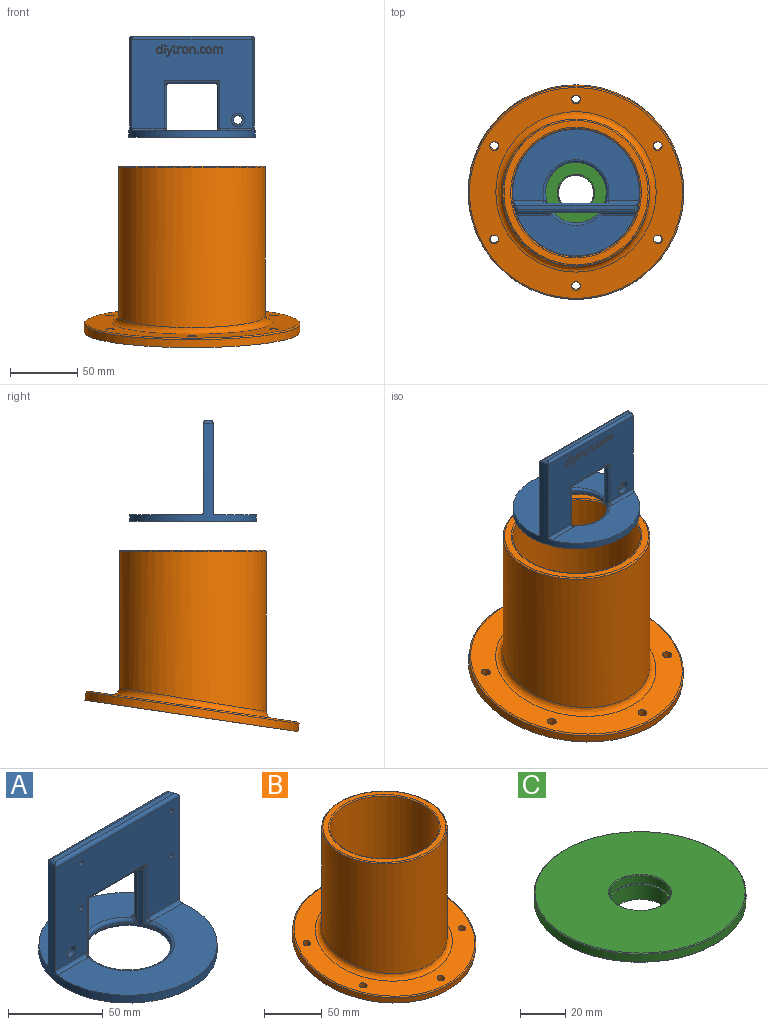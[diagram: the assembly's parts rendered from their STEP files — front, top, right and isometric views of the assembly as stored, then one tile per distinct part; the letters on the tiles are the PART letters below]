
ASSEMBLY  parts=3 mates=2
PART A: 256 faces, bbox 94x94x75 mm
  f0: plane 89.08x66mm, normal (0,1,0), area 4240.6mm2, adj f3,f12,f13,f17,f39,f42,f43,f52
  f1: plane 92.63x66.23mm, normal (0,-1,0), area 4484.7mm2, adj f3,f9,f11,f16,f29,f31,f33,f35
  f2: plane 87.64x30.79mm, normal (0,0,1), area 1726.6mm2, adj f3,f14,f43,f44,f52,f53
  f3: cylinder r=47mm len=94mm, axis (0,0,-1), area 2463.1mm2, adj f0,f1,f2,f4,f5,f37,f38,f43
  f4: plane 94x53mm, normal (0,0,1), area 2798.4mm2, adj f3,f10,f46,f49
  f5: plane 94x94mm, normal (0,0,-1), area 5054mm2, adj f3,f15
  f6: plane 87.75x3mm, normal (0,0,1), area 261mm2, adj f36,f37,f38,f39
  f7: cylinder r=22.5mm len=45mm, axis (0,0,-1), area 360.8mm2, adj f9,f10,f11,f12,f13,f14,f15,f20
  f8: plane 35.79x3mm, normal (0,0,-1), area 103mm2, adj f16,f17,f19,f20,f25,f26
  f9: cylinder r=2mm len=39mm, axis (0,0,-1), area 80mm2, adj f1,f7,f22,f48
  f10: torus R=24.5mm, axis (0,0,1), area 274.5mm2, adj f4,f7,f47,f48,f50,f51
  f11: cylinder r=2mm len=39mm, axis (0,0,-1), area 80mm2, adj f1,f7,f23,f51
  f12: cylinder r=2mm len=39mm, axis (0,0,-1), area 140.9mm2, adj f0,f7,f26,f27,f53,f54
  f13: cylinder r=2mm len=39mm, axis (0,0,-1), area 140.9mm2, adj f0,f7,f18,f19,f44,f45
  f14: torus R=24.5mm, axis (0,0,1), area 131.6mm2, adj f2,f7,f45,f54
  f15: torus R=24.5mm, axis (0,0,1), area 458.5mm2, adj f5,f7
  f16: cylinder r=2mm len=44.73mm, axis (1,0,0), area 124.2mm2, adj f1,f8,f21,f22,f23,f24
  f17: cylinder r=2mm len=41.53mm, axis (-1,0,0), area 114.5mm2, adj f0,f8,f18,f27
  f18: bspline ~4x4mm, area 7.6mm2, adj f13,f17,f19
  f19: torus R=4mm, axis (0,0,1), area 4.8mm2, adj f8,f13,f18,f20
  f20: torus R=20.5mm, axis (0,0,1), area 3.4mm2, adj f7,f8,f19,f21
  f21: bspline ~3.34x3.27mm, area 4.5mm2, adj f7,f16,f20,f22
  f22: bspline ~3.75x3.75mm, area 5.4mm2, adj f9,f16,f21
  f23: bspline ~3.75x3.75mm, area 5.4mm2, adj f11,f16,f24
  f24: bspline ~3.34x3.27mm, area 4.5mm2, adj f7,f16,f23,f25
  f25: torus R=20.5mm, axis (0,0,1), area 3.4mm2, adj f7,f8,f24,f26
  f26: torus R=4mm, axis (0,0,1), area 4.8mm2, adj f8,f12,f25,f27
  f27: bspline ~4x4mm, area 7.6mm2, adj f12,f17,f26
  f28: cone r=0mm half-angle=59deg, axis (0,-1,0), area 8.8mm2, adj f29
  f29: cylinder r=1.55mm len=4mm, axis (0,-1,0), area 39mm2, adj f1,f28
  f30: cone r=0mm half-angle=59deg, axis (0,-1,0), area 8.8mm2, adj f31
  f31: cylinder r=1.55mm len=4mm, axis (0,-1,0), area 39mm2, adj f1,f30
  f32: cone r=0mm half-angle=59deg, axis (0,-1,0), area 8.8mm2, adj f33
  f33: cylinder r=1.55mm len=4mm, axis (0,-1,0), area 39mm2, adj f1,f32
  f34: cone r=0mm half-angle=59deg, axis (0,-1,0), area 8.8mm2, adj f35
  f35: cylinder r=1.55mm len=4mm, axis (0,-1,0), area 39mm2, adj f1,f34
  f36: cylinder r=2mm len=92.63mm, axis (-1,0,0), area 285.5mm2, adj f1,f6,f37,f38
  f37: torus R=45mm, axis (0,0,1), area 18mm2, adj f3,f6,f36,f39
  f38: torus R=45mm, axis (0,0,1), area 18mm2, adj f3,f6,f36,f39
  f39: cylinder r=2mm len=89.08mm, axis (1,0,0), area 276.6mm2, adj f0,f6,f37,f38
  f40: cylinder r=3.25mm len=6.5mm, axis (0,1,0), area 61.3mm2, adj f1,f41
  f41: plane 10x10mm, normal (0,1,0), area 45.4mm2, adj f40,f42
  f42: cylinder r=5mm len=10mm, axis (0,1,0), area 125.7mm2, adj f0,f41
  f43: cylinder r=2mm len=23.78mm, axis (1,0,0), area 73.9mm2, adj f0,f2,f3,f44
  f44: torus R=4mm, axis (0,0,1), area 5.5mm2, adj f2,f13,f43,f45
  f45: bspline ~4.41x4mm, area 7.5mm2, adj f13,f14,f44
  f46: cylinder r=2mm len=22.86mm, axis (-1,0,0), area 71.3mm2, adj f1,f3,f4,f47
  f47: bspline ~3.17x2.31mm, area 3mm2, adj f1,f10,f46,f48
  f48: bspline ~3.94x3.05mm, area 5.9mm2, adj f9,f10,f47
  f49: cylinder r=2mm len=22.86mm, axis (-1,0,0), area 71.3mm2, adj f1,f3,f4,f50
  f50: bspline ~3.17x2.31mm, area 3mm2, adj f1,f10,f49,f51
  f51: bspline ~3.94x3.05mm, area 5.9mm2, adj f10,f11,f50
  f52: cylinder r=2mm len=23.78mm, axis (1,0,0), area 73.9mm2, adj f0,f2,f3,f53
  f53: torus R=4mm, axis (0,0,1), area 5.5mm2, adj f2,f12,f52,f54
  f54: bspline ~4.41x4mm, area 7.5mm2, adj f12,f14,f53
  f55: plane 1x0.72mm, normal (0,0,1), area 0.7mm2, adj f0,f56,f58,f59
  f56: plane 4.77x1mm, normal (1,0,0), area 4.8mm2, adj f0,f55,f57,f59
  f57: plane 1x0.72mm, normal (0,0,-1), area 0.7mm2, adj f0,f56,f58,f59
  f58: plane 4.77x1mm, normal (-1,0,0), area 4.8mm2, adj f0,f55,f57,f59
  f59: plane 4.77x0.72mm, normal (0,1,0), area 3.4mm2, adj f55,f56,f57,f58
  f60: extruded ~1.39x1mm, area 1.5mm2, adj f61,f76,f77,f253
  f61: extruded ~1.39x1mm, area 1.5mm2, adj f60,f62,f77,f253
  f62: extruded ~1.07x1mm, area 1.2mm2, adj f61,f63,f77,f253
  f63: extruded ~1.09x1mm, area 1.2mm2, adj f62,f64,f77,f253
  f64: extruded ~1.38x1mm, area 1.5mm2, adj f63,f65,f77,f253
  f65: extruded ~1.4x1mm, area 1.5mm2, adj f64,f66,f77,f253
  f66: extruded ~1.08x1mm, area 1.2mm2, adj f65,f76,f77,f253
  f67: extruded ~1.82x1mm, area 2mm2, adj f0,f68,f75,f77
  f68: extruded ~1.8x1mm, area 1.9mm2, adj f0,f67,f69,f77
  f69: extruded ~1.59x1mm, area 1.8mm2, adj f0,f68,f70,f77
  f70: extruded ~1.62x1mm, area 1.8mm2, adj f0,f69,f71,f77
  f71: extruded ~1.82x1mm, area 2mm2, adj f0,f70,f72,f77
  f72: extruded ~1.32x1mm, area 1.4mm2, adj f0,f71,f73,f77
  f73: extruded ~1x0.86mm, area 1.2mm2, adj f0,f72,f74,f77
  f74: extruded ~1.14x1mm, area 1.2mm2, adj f0,f73,f75,f77
  f75: extruded ~1.62x1mm, area 1.8mm2, adj f0,f67,f74,f77
  f76: extruded ~1.07x1mm, area 1.2mm2, adj f60,f66,f77,f253
  f77: plane 4.95x4.38mm, normal (0,1,0), area 8.7mm2, adj f60,f61,f62,f63,f64,f65,f66,f67
  f78: extruded ~1.39x1mm, area 1.5mm2, adj f79,f94,f95,f254
  f79: extruded ~1.39x1mm, area 1.5mm2, adj f78,f80,f95,f254
  f80: extruded ~1.07x1mm, area 1.2mm2, adj f79,f81,f95,f254
  f81: extruded ~1.09x1mm, area 1.2mm2, adj f80,f82,f95,f254
  f82: extruded ~1.38x1mm, area 1.5mm2, adj f81,f83,f95,f254
  f83: extruded ~1.4x1mm, area 1.5mm2, adj f82,f84,f95,f254
  f84: extruded ~1.08x1mm, area 1.2mm2, adj f83,f94,f95,f254
  f85: extruded ~1.82x1mm, area 2mm2, adj f0,f86,f93,f95
  f86: extruded ~1.8x1mm, area 1.9mm2, adj f0,f85,f87,f95
  f87: extruded ~1.59x1mm, area 1.8mm2, adj f0,f86,f88,f95
  f88: extruded ~1.62x1mm, area 1.8mm2, adj f0,f87,f89,f95
  f89: extruded ~1.82x1mm, area 2mm2, adj f0,f88,f90,f95
  f90: extruded ~1.32x1mm, area 1.4mm2, adj f0,f89,f91,f95
  f91: extruded ~1x0.86mm, area 1.2mm2, adj f0,f90,f92,f95
  f92: extruded ~1.14x1mm, area 1.2mm2, adj f0,f91,f93,f95
  f93: extruded ~1.62x1mm, area 1.8mm2, adj f0,f85,f92,f95
  f94: extruded ~1.07x1mm, area 1.2mm2, adj f78,f84,f95,f254
  f95: plane 4.95x4.38mm, normal (0,1,0), area 8.7mm2, adj f78,f79,f80,f81,f82,f83,f84,f85
  f96: extruded ~1.07x1mm, area 1.2mm2, adj f97,f119,f120,f255
  f97: extruded ~1x0.98mm, area 1.1mm2, adj f96,f98,f120,f255
  f98: extruded ~1.38x1mm, area 1.4mm2, adj f97,f99,f120,f255
  f99: extruded ~1.4x1mm, area 1.5mm2, adj f98,f100,f120,f255
  f100: extruded ~1x0.97mm, area 1.1mm2, adj f99,f101,f120,f255
  f101: extruded ~1.08x1mm, area 1.2mm2, adj f100,f102,f120,f255
  f102: extruded ~1.45x1mm, area 1.5mm2, adj f101,f103,f120,f255
  f103: plane 1x0.15mm, normal (-1,0,0), area 0.2mm2, adj f102,f119,f120,f255
  f104: plane 1x0.04mm, normal (0,0,1), area 0mm2, adj f0,f105,f118,f120
  f105: plane 1x0.64mm, normal (-0.99,0,0.15), area 0.6mm2, adj f0,f104,f106,f120
  f106: plane 1x0.59mm, normal (0,0,1), area 0.6mm2, adj f0,f105,f107,f120
  f107: plane 6.77x1mm, normal (1,0,0), area 6.8mm2, adj f0,f106,f108,f120
  f108: plane 1x0.72mm, normal (0,0,-1), area 0.7mm2, adj f0,f107,f109,f120
  f109: plane 1.94x1mm, normal (-1,0,0), area 1.9mm2, adj f0,f108,f110,f120
  f110: plane 1x0.34mm, normal (-1,0,0.05), area 0.3mm2, adj f0,f109,f111,f120
  f111: plane 1x0.34mm, normal (-1,0,0.09), area 0.3mm2, adj f0,f110,f112,f120
  f112: plane 1x0.06mm, normal (0,0,-1), area 0.1mm2, adj f0,f111,f113,f120
  f113: extruded ~1.49x1mm, area 1.7mm2, adj f0,f112,f114,f120
  f114: extruded ~1.45x1mm, area 1.7mm2, adj f0,f113,f115,f120
  f115: extruded ~1.83x1mm, area 1.9mm2, adj f0,f114,f116,f120
  f116: extruded ~1.82x1mm, area 1.9mm2, adj f0,f115,f117,f120
  f117: extruded ~1.46x1mm, area 1.6mm2, adj f0,f116,f118,f120
  f118: extruded ~1.5x1mm, area 1.7mm2, adj f0,f104,f117,f120
  f119: extruded ~1.3x1mm, area 1.4mm2, adj f96,f103,f120,f255
  f120: plane 6.86x4.2mm, normal (0,1,0), area 11.1mm2, adj f96,f97,f98,f99,f100,f101,f102,f103
  f121: plane 3.1x1mm, normal (-1,0,0), area 3.1mm2, adj f0,f122,f148,f149
  f122: plane 1x0.72mm, normal (0,0,1), area 0.7mm2, adj f0,f121,f123,f149
  f123: plane 3.11x1mm, normal (1,0,0), area 3.1mm2, adj f0,f122,f124,f149
  f124: extruded ~1.33x1mm, area 1.4mm2, adj f0,f123,f125,f149
  f125: extruded ~1.21x1mm, area 1.3mm2, adj f0,f124,f126,f149
  f126: extruded ~1x0.92mm, area 1mm2, adj f0,f125,f127,f149
  f127: extruded ~1x0.62mm, area 0.9mm2, adj f0,f126,f128,f149
  f128: plane 1x0.04mm, normal (0,0,-1), area 0mm2, adj f0,f127,f129,f149
  f129: extruded ~1.46x1mm, area 1.8mm2, adj f0,f128,f130,f149
  f130: extruded ~1x0.83mm, area 0.9mm2, adj f0,f129,f131,f149
  f131: extruded ~1x0.58mm, area 0.8mm2, adj f0,f130,f132,f149
  f132: plane 1x0.04mm, normal (0,0,-1), area 0mm2, adj f0,f131,f133,f149
  f133: plane 1x0.65mm, normal (0.98,0,-0.18), area 0.7mm2, adj f0,f132,f134,f149
  f134: plane 1x0.59mm, normal (0,0,-1), area 0.6mm2, adj f0,f133,f135,f149
  f135: plane 4.77x1mm, normal (-1,0,0), area 4.8mm2, adj f0,f134,f136,f149
  f136: plane 1x0.72mm, normal (0,0,1), area 0.7mm2, adj f0,f135,f137,f149
  f137: plane 2.5x1mm, normal (1,0,0), area 2.5mm2, adj f0,f136,f138,f149
  f138: extruded ~1.33x1mm, area 1.4mm2, adj f0,f137,f139,f149
  f139: extruded ~1x0.99mm, area 1.1mm2, adj f0,f138,f140,f149
  f140: extruded ~1x0.76mm, area 0.8mm2, adj f0,f139,f141,f149
  f141: extruded ~1x0.86mm, area 0.9mm2, adj f0,f140,f142,f149
  f142: plane 3.1x1mm, normal (-1,0,0), area 3.1mm2, adj f0,f141,f143,f149
  f143: plane 1x0.72mm, normal (0,0,1), area 0.7mm2, adj f0,f142,f144,f149
  f144: plane 2.66x1mm, normal (1,0,0), area 2.7mm2, adj f0,f143,f145,f149
  f145: extruded ~1.19x1mm, area 1.3mm2, adj f0,f144,f146,f149
  f146: extruded ~1x1mm, area 1.1mm2, adj f0,f145,f147,f149
  f147: extruded ~1x0.76mm, area 0.8mm2, adj f0,f146,f148,f149
  f148: extruded ~1x0.86mm, area 0.9mm2, adj f0,f121,f147,f149
  f149: plane 6.8x4.86mm, normal (0,1,0), area 12.9mm2, adj f121,f122,f123,f124,f125,f126,f127,f128
  f150: extruded ~1.6x1mm, area 1.8mm2, adj f0,f151,f164,f165
  f151: extruded ~1.21x1mm, area 1.2mm2, adj f0,f150,f152,f165
  f152: plane 1x0.64mm, normal (1,0,0), area 0.6mm2, adj f0,f151,f153,f165
  f153: extruded ~1.22x1mm, area 1.3mm2, adj f0,f152,f154,f165
  f154: extruded ~1.05x1mm, area 1.2mm2, adj f0,f153,f155,f165
  f155: extruded ~1.35x1mm, area 1.4mm2, adj f0,f154,f156,f165
  f156: extruded ~1.85x1.45mm, area 2.7mm2, adj f0,f155,f157,f165
  f157: extruded ~1x0.5mm, area 0.5mm2, adj f0,f156,f158,f165
  f158: extruded ~1x0.52mm, area 0.5mm2, adj f0,f157,f159,f165
  f159: plane 1x0.61mm, normal (0.94,0,0.34), area 0.7mm2, adj f0,f158,f160,f165
  f160: extruded ~1x0.54mm, area 0.6mm2, adj f0,f159,f161,f165
  f161: extruded ~1x0.69mm, area 0.7mm2, adj f0,f160,f162,f165
  f162: extruded ~1.64x1mm, area 1.8mm2, adj f0,f161,f163,f165
  f163: extruded ~1.85x1mm, area 2mm2, adj f0,f162,f164,f165
  f164: extruded ~1.81x1mm, area 1.9mm2, adj f0,f150,f163,f165
  f165: plane 4.95x3.45mm, normal (0,1,0), area 6mm2, adj f150,f151,f152,f153,f154,f155,f156,f157
  f166: extruded ~1x0.44mm, area 0.5mm2, adj f0,f167,f173,f174
  f167: extruded ~1x0.45mm, area 0.5mm2, adj f0,f166,f168,f174
  f168: extruded ~1x0.37mm, area 0.4mm2, adj f0,f167,f169,f174
  f169: extruded ~1x0.39mm, area 0.4mm2, adj f0,f168,f170,f174
  f170: extruded ~1x0.44mm, area 0.5mm2, adj f0,f169,f171,f174
  f171: extruded ~1x0.44mm, area 0.5mm2, adj f0,f170,f172,f174
  f172: extruded ~1x0.39mm, area 0.4mm2, adj f0,f171,f173,f174
  f173: extruded ~1x0.38mm, area 0.4mm2, adj f0,f166,f172,f174
  f174: plane 1.18x1.05mm, normal (0,1,0), area 1mm2, adj f166,f167,f168,f169,f170,f171,f172,f173
  f175: plane 3.09x1mm, normal (-1,0,0), area 3.1mm2, adj f0,f176,f191,f192
  f176: plane 1x0.72mm, normal (0,0,1), area 0.7mm2, adj f0,f175,f177,f192
  f177: plane 3.11x1mm, normal (1,0,0), area 3.1mm2, adj f0,f176,f178,f192
  f178: extruded ~1.33x1mm, area 1.4mm2, adj f0,f177,f179,f192
  f179: extruded ~1.3x1mm, area 1.4mm2, adj f0,f178,f180,f192
  f180: extruded ~1x0.89mm, area 0.9mm2, adj f0,f179,f181,f192
  f181: extruded ~1x0.62mm, area 0.8mm2, adj f0,f180,f182,f192
  f182: plane 1x0.04mm, normal (0,0,-1), area 0mm2, adj f0,f181,f183,f192
  f183: plane 1x0.65mm, normal (0.98,0,-0.18), area 0.7mm2, adj f0,f182,f184,f192
  f184: plane 1x0.59mm, normal (0,0,-1), area 0.6mm2, adj f0,f183,f185,f192
  f185: plane 4.77x1mm, normal (-1,0,0), area 4.8mm2, adj f0,f184,f186,f192
  f186: plane 1x0.72mm, normal (0,0,1), area 0.7mm2, adj f0,f185,f187,f192
  f187: plane 2.5x1mm, normal (1,0,0), area 2.5mm2, adj f0,f186,f188,f192
  f188: extruded ~1.34x1mm, area 1.4mm2, adj f0,f187,f189,f192
  f189: extruded ~1.1x1mm, area 1.2mm2, adj f0,f188,f190,f192
  f190: extruded ~1x0.83mm, area 0.9mm2, adj f0,f189,f191,f192
  f191: extruded ~1x0.87mm, area 0.9mm2, adj f0,f175,f190,f192
  f192: plane 4.86x3.99mm, normal (0,1,0), area 8.2mm2, adj f175,f176,f177,f178,f179,f180,f181,f182
  f193: extruded ~1x0.57mm, area 0.6mm2, adj f0,f194,f205,f206
  f194: extruded ~1x0.82mm, area 0.9mm2, adj f0,f193,f195,f206
  f195: extruded ~1x0.72mm, area 1mm2, adj f0,f194,f196,f206
  f196: plane 1x0.04mm, normal (0,0,-1), area 0mm2, adj f0,f195,f197,f206
  f197: plane 1x0.88mm, normal (1,0,-0.09), area 0.9mm2, adj f0,f196,f198,f206
  f198: plane 1x0.6mm, normal (0,0,-1), area 0.6mm2, adj f0,f197,f199,f206
  f199: plane 4.77x1mm, normal (-1,0,0), area 4.8mm2, adj f0,f198,f200,f206
  f200: plane 1x0.72mm, normal (0,0,1), area 0.7mm2, adj f0,f199,f201,f206
  f201: plane 2.56x1mm, normal (1,0,0), area 2.6mm2, adj f0,f200,f202,f206
  f202: extruded ~1.17x1mm, area 1.3mm2, adj f0,f201,f203,f206
  f203: extruded ~1x0.99mm, area 1.1mm2, adj f0,f202,f204,f206
  f204: extruded ~1x0.52mm, area 0.5mm2, adj f0,f203,f205,f206
  f205: plane 1x0.67mm, normal (0.99,0,0.15), area 0.7mm2, adj f0,f193,f204,f206
  f206: plane 4.86x2.75mm, normal (0,1,0), area 4.7mm2, adj f193,f194,f195,f196,f197,f198,f199,f200
  f207: extruded ~1x0.37mm, area 0.4mm2, adj f0,f208,f225,f226
  f208: extruded ~1x0.56mm, area 0.6mm2, adj f0,f207,f209,f226
  f209: extruded ~1x0.66mm, area 0.7mm2, adj f0,f208,f210,f226
  f210: plane 2.81x1mm, normal (1,0,0), area 2.8mm2, adj f0,f209,f211,f226
  f211: plane 1.38x1mm, normal (0,0,1), area 1.4mm2, adj f0,f210,f212,f226
  f212: plane 1x0.56mm, normal (1,0,0), area 0.6mm2, adj f0,f211,f213,f226
  f213: plane 1.38x1mm, normal (0,0,-1), area 1.4mm2, adj f0,f212,f214,f226
  f214: plane 1.11x1mm, normal (1,0,0), area 1.1mm2, adj f0,f213,f215,f226
  f215: plane 1x0.42mm, normal (0,0,-1), area 0.4mm2, adj f0,f214,f216,f226
  f216: plane 1.02x1mm, normal (-0.96,0,-0.29), area 1.1mm2, adj f0,f215,f217,f226
  f217: plane 1x0.68mm, normal (-0.4,0,-0.92), area 0.7mm2, adj f0,f216,f218,f226
  f218: plane 1x0.35mm, normal (-1,0,0), area 0.3mm2, adj f0,f217,f219,f226
  f219: plane 1x0.68mm, normal (0,0,1), area 0.7mm2, adj f0,f218,f220,f226
  f220: plane 2.84x1mm, normal (-1,0,0), area 2.8mm2, adj f0,f219,f221,f226
  f221: extruded ~1.46x1.38mm, area 2.3mm2, adj f0,f220,f222,f226
  f222: extruded ~1x0.41mm, area 0.4mm2, adj f0,f221,f223,f226
  f223: extruded ~1x0.35mm, area 0.4mm2, adj f0,f222,f224,f226
  f224: plane 1x0.55mm, normal (1,0,0), area 0.6mm2, adj f0,f223,f225,f226
  f225: extruded ~1x0.28mm, area 0.3mm2, adj f0,f207,f224,f226
  f226: plane 5.96x2.82mm, normal (0,1,0), area 5.9mm2, adj f207,f208,f209,f210,f211,f212,f213,f214
  f227: plane 1x0.78mm, normal (0,0,-1), area 0.8mm2, adj f0,f228,f242,f243
  f228: plane 4.8x1.93mm, normal (-0.93,0,0.37), area 5.2mm2, adj f0,f227,f229,f243
  f229: plane 1x0.68mm, normal (-0.93,0,-0.37), area 0.7mm2, adj f0,f228,f230,f243
  f230: extruded ~1.06x1mm, area 1.5mm2, adj f0,f229,f231,f243
  f231: extruded ~1x0.54mm, area 0.5mm2, adj f0,f230,f232,f243
  f232: plane 1x0.58mm, normal (-1,0,0), area 0.6mm2, adj f0,f231,f233,f243
  f233: extruded ~1x0.65mm, area 0.7mm2, adj f0,f232,f234,f243
  f234: extruded ~1x1mm, area 1.1mm2, adj f0,f233,f235,f243
  f235: extruded ~1.14x1mm, area 1.4mm2, adj f0,f234,f236,f243
  f236: plane 5.43x2.05mm, normal (0.94,0,0.35), area 5.8mm2, adj f0,f235,f237,f243
  f237: plane 1x0.77mm, normal (0,0,-1), area 0.8mm2, adj f0,f236,f238,f243
  f238: extruded ~3.31x1.18mm, area 3.5mm2, adj f0,f237,f239,f243
  f239: extruded ~1x0.76mm, area 0.8mm2, adj f0,f238,f240,f243
  f240: plane 1x0.04mm, normal (0,0,-1), area 0mm2, adj f0,f239,f241,f243
  f241: extruded ~1.35x1mm, area 1.4mm2, adj f0,f240,f242,f243
  f242: plane 2.72x1.04mm, normal (0.93,0,-0.36), area 2.9mm2, adj f0,f227,f241,f243
  f243: plane 6.91x4.48mm, normal (0,1,0), area 8.8mm2, adj f227,f228,f229,f230,f231,f232,f233,f234
  f244: extruded ~1x0.36mm, area 0.4mm2, adj f0,f245,f251,f252
  f245: extruded ~1x0.36mm, area 0.4mm2, adj f0,f244,f246,f252
  f246: extruded ~1x0.31mm, area 0.3mm2, adj f0,f245,f247,f252
  f247: extruded ~1x0.3mm, area 0.3mm2, adj f0,f246,f248,f252
  f248: extruded ~1x0.36mm, area 0.4mm2, adj f0,f247,f249,f252
  f249: extruded ~1x0.36mm, area 0.4mm2, adj f0,f248,f250,f252
  f250: extruded ~1x0.3mm, area 0.3mm2, adj f0,f249,f251,f252
  f251: extruded ~1x0.31mm, area 0.3mm2, adj f0,f244,f250,f252
  f252: plane 0.96x0.85mm, normal (0,1,0), area 0.7mm2, adj f244,f245,f246,f247,f248,f249,f250,f251
  f253: plane 3.73x2.89mm, normal (0,1,0), area 8.9mm2, adj f60,f61,f62,f63,f64,f65,f66,f76
  f254: plane 3.73x2.89mm, normal (0,1,0), area 8.9mm2, adj f78,f79,f80,f81,f82,f83,f84,f94
  f255: plane 3.73x2.72mm, normal (0,1,0), area 8.6mm2, adj f96,f97,f98,f99,f100,f101,f102,f103
PART B: 20 faces, bbox 173.2x171.3x134.6 mm
  f0: cylinder r=3.3mm len=7.89mm, axis (0,0.15,-0.99), area 145.1mm2, adj f10,f11
  f1: cylinder r=3.3mm len=7.89mm, axis (0,0.15,-0.99), area 145.1mm2, adj f10,f11
  f2: cylinder r=3.3mm len=7.89mm, axis (0,0.15,-0.99), area 145.1mm2, adj f10,f11
  f3: cylinder r=3.3mm len=7.89mm, axis (0,0.15,-0.99), area 145.1mm2, adj f10,f11
  f4: cylinder r=3.3mm len=7.89mm, axis (0,0.15,-0.99), area 145.1mm2, adj f10,f11
  f5: bspline ~94.64x94.14mm, area 3660.7mm2, adj f7,f8
  f6: plane 95x95mm, normal (0,0,1), area 2152.4mm2, adj f7,f15
  f7: torus R=39.64mm, axis (0,0,1), area 553.9mm2, adj f5,f6
  f8: cylinder r=47.5mm len=95mm, axis (0,0,1), area 2731mm2, adj f5,f11
  f9: cylinder r=80mm len=160mm, axis (0,0.15,-0.99), area 3015.9mm2, adj f11,f17
  f10: plane 158x156.31mm, normal (0,-0.15,0.99), area 8159mm2, adj f0,f1,f2,f3,f4,f14,f17,f18
  f11: plane 160x158.29mm, normal (0,0.15,-0.99), area 12736mm2, adj f0,f1,f2,f3,f4,f8,f9,f18
  f12: cylinder r=54.5mm len=118.72mm, axis (0,0,-1), area 40655.3mm2, adj f14,f19
  f13: plane 107x107mm, normal (0,0,1), area 1602.2mm2, adj f16,f19
  f14: bspline ~118.94x118.88mm, area 2794.5mm2, adj f10,f12
  f15: cylinder r=47.5mm len=100.93mm, axis (0,0,1), area 30121.2mm2, adj f6,f16
  f16: torus R=48.5mm, axis (0,0,1), area 472.4mm2, adj f13,f15
  f17: torus R=79mm, axis (0,0.15,-0.99), area 786mm2, adj f9,f10
  f18: cylinder r=3.3mm len=7.89mm, axis (0,0.15,-0.99), area 145.1mm2, adj f10,f11
  f19: torus R=53.5mm, axis (0,0,1), area 534.3mm2, adj f12,f13
PART C: 19 faces, bbox 94x94x13 mm
  f0: plane 93.2x93.2mm, normal (0,0,-1), area 5807.3mm2, adj f6,f9,f10,f11,f12,f13,f14,f15
  f1: cylinder r=47mm len=94mm, axis (0,0,-1), area 1240.3mm2, adj f6,f7
  f2: plane 93.2x93.2mm, normal (0,0,1), area 6215.2mm2, adj f5,f7
  f3: cylinder r=13.5mm len=27mm, axis (0,0,-1), area 356.3mm2, adj f4,f5
  f4: cone r=13.9mm half-angle=45deg, axis (0,0,-1), area 48.7mm2, adj f3,f8
  f5: cone r=13.5mm half-angle=45deg, axis (0,0,1), area 48.7mm2, adj f2,f3
  f6: cone r=47mm half-angle=45deg, axis (0,0,1), area 166.3mm2, adj f0,f1
  f7: cone r=46.6mm half-angle=45deg, axis (0,0,-1), area 166.3mm2, adj f1,f2
  f8: plane 27.8x27.8mm, normal (0,0,1), area 76.1mm2, adj f4,f16
  f9: plane 14.16x8mm, normal (0.21,-0.98,0), area 116mm2, adj f0,f10,f17,f18
  f10: plane 12.21x8mm, normal (-0.54,-0.84,0), area 116mm2, adj f0,f9,f11,f18
  f11: plane 14.16x8mm, normal (-0.98,-0.21,0), area 116mm2, adj f0,f10,f12,f18
  f12: plane 12.21x8mm, normal (-0.84,0.54,0), area 116mm2, adj f0,f11,f13,f18
  f13: plane 14.16x8mm, normal (-0.21,0.98,0), area 116mm2, adj f0,f12,f14,f18
  f14: plane 12.21x8mm, normal (0.54,0.84,0), area 116mm2, adj f0,f13,f15,f18
  f15: plane 14.16x8mm, normal (0.98,0.21,0), area 116mm2, adj f0,f14,f17,f18
  f16: cylinder r=13mm len=26mm, axis (0,0,1), area 653.5mm2, adj f8,f18
  f17: plane 12.21x8mm, normal (0.84,-0.54,0), area 116mm2, adj f0,f9,f15,f18
  f18: plane 37.3x37.3mm, normal (0,0,-1), area 483.9mm2, adj f9,f10,f11,f12,f13,f14,f15,f16
PLACE A rot(axis=(0,0,-1),180deg) t=(185.39,-20.19,107.21)mm
PLACE B t=(185.39,-220.2,-21.48)mm
PLACE C t=(185.39,-20.19,-6.09)mm
MATE cylindrical B.f7 <-> C.f1  axis (0,0,-1) through (185.39,-20.19,-16.09)mm
MATE cylindrical A.f3 <-> C.f1  axis (0,0,1) through (185.39,-20.19,107.21)mm
